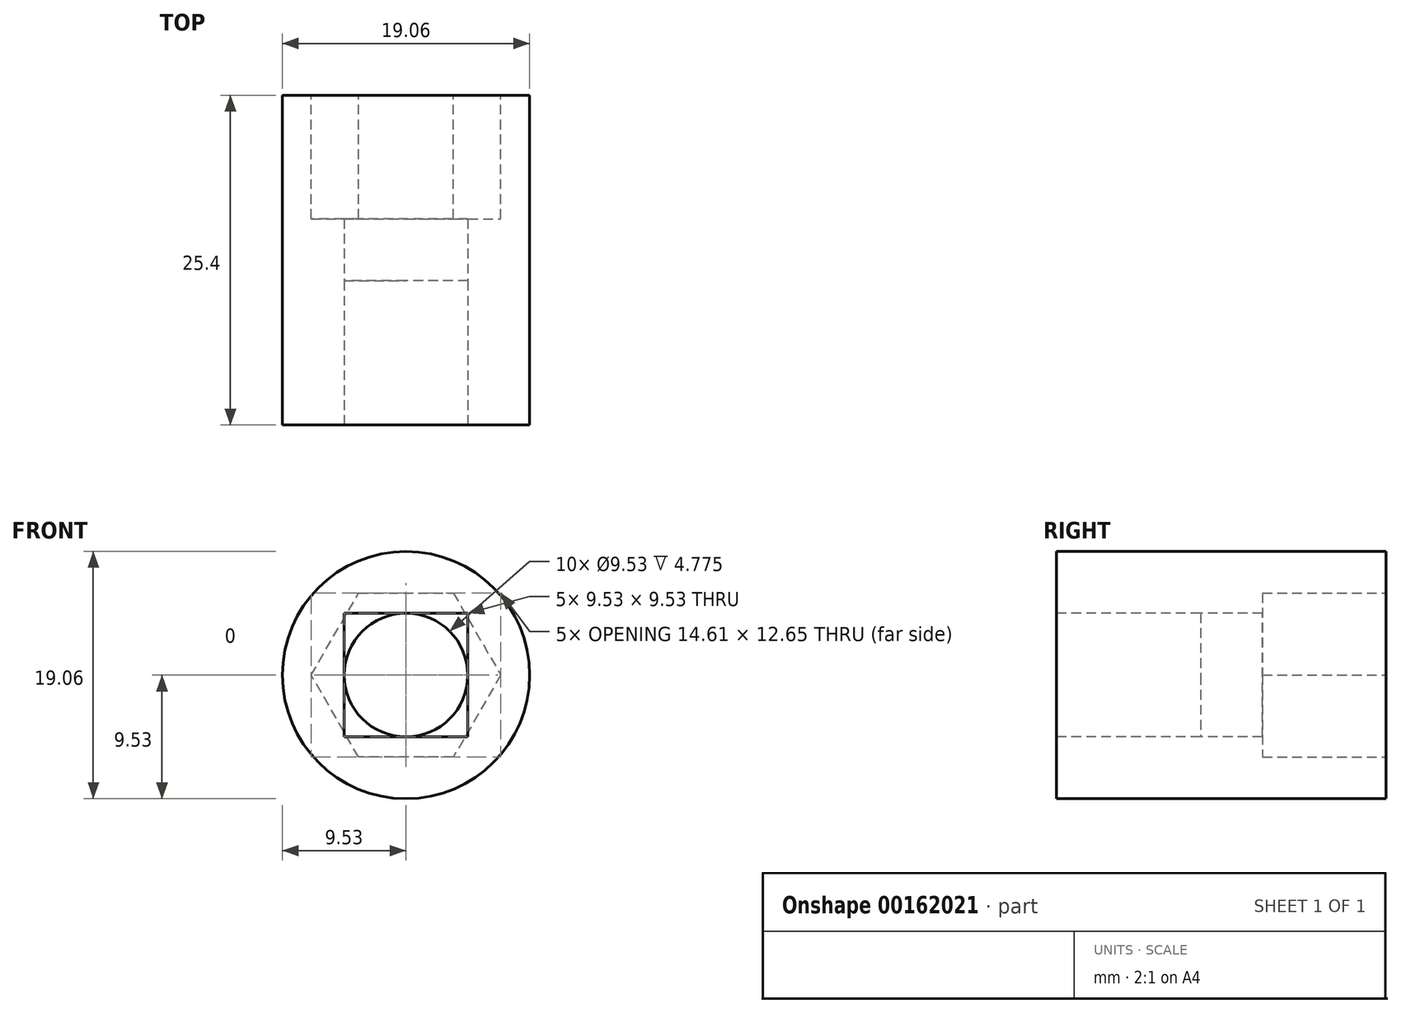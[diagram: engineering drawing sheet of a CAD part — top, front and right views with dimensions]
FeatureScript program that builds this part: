
annotation { "Feature Type Name" : "Feature", "Feature Type Description" : "" }
export const myFeature = defineFeature(function(context is Context, id is Id, definition is map)
    precondition{}
    {
        {
            var Q0;
            Q0=qCreatedBy(makeId("Front.planeOp"),FACE);
            var sketch = newSketch(context, id + "F0", { "sketchPlane" : qUnion([Q0])});
            skCircle(sketch, "E0", {"center": v(0, 0) * mm, "radius": 9.53 * mm});
            skSolve(sketch);
        }
        {
            var Q0;
            Q0 = qSketchRegion(id + "F0", true);
            extrude(context, id + "F1", {"entities" : qUnion([Q0]), "depth" : 25.4 * mm});
        }
        {
            var Q0;
            Q0=makeQuery(id+"F1.opExtrude","CAP_FACE",FACE,{"disambiguationData":[OSD([sQuery(id+"F0.wireOp",EDGE,"E0")])],"isStart":false});
            var sketch = newSketch(context, id + "F2", { "sketchPlane" : qUnion([Q0])});
            skLineSegment(sketch, "E1.bottom", {"start": v(4.76, 4.76) * mm, "end": v(-4.76, 4.76) * mm});
            skLineSegment(sketch, "E1.top", {"start": v(4.76, -4.76) * mm, "end": v(-4.76, -4.76) * mm});
            skLineSegment(sketch, "E1.left", {"start": v(4.76, 4.76) * mm, "end": v(4.76, -4.76) * mm});
            skLineSegment(sketch, "E1.right", {"start": v(-4.76, 4.76) * mm, "end": v(-4.76, -4.76) * mm});
            skPoint(sketch, "E1.middle", {"position": v(0, 0) * mm});
            skCircle(sketch, "E2", {"center": v(0, 0) * mm, "radius": 4.76 * mm});
            skSolve(sketch);
        }
        {
            var Q0;
            {var subQ0=sQuery(id+"F2.wireOp",EDGE,"E2");var subQ1=makeQuery(id+"F2.imprint","INTERSECT",VERTEX,{"derivedFrom":[sQuery(id+"F2.wireOp",EDGE,"E1.bottom"),subQ0]});Q0=makeQuery(id+"F2.imprint","IMPRINT",FACE,{"disambiguationData":[TD([[makeQuery(id+"F2.imprint","IMPRINT",EDGE,{"disambiguationData":[TD([[subQ1,1.0]])],"derivedFrom":subQ0}),1.0]])]});}
            var Q1;
            Q1=sQuery(id+"F2.wireOp",EDGE,"E2");
            extrude(context, id + "F3", {"entities" : qUnion([Q0]), "operationType" : NewBodyOperationType.REMOVE, "surfaceEntities" : qUnion([Q1]), "endBound" : BoundingType.THROUGH_ALL, "oppositeDirection" : true, "depth" : 25.4 * mm});
        }
        {
            var Q0;
            Q0 = qSketchRegion(id + "F2", true);
            extrude(context, id + "F4", {"entities" : qUnion([Q0]), "operationType" : NewBodyOperationType.REMOVE, "oppositeDirection" : true, "depth" : 11.1 * mm});
        }
        {
            var Q0;
            Q0=qCreatedBy(makeId("Front.planeOp"),FACE);
            var sketch = newSketch(context, id + "F5", { "sketchPlane" : qUnion([Q0])});
            skCircle(sketch, "E3.cCircle", {"center": v(0, 0) * mm, "radius": 6.32 * mm, "construction": true});
            skLineSegment(sketch, "E3.0", {"start": v(-3.65, 6.32) * mm, "end": v(3.65, 6.32) * mm});
            skLineSegment(sketch, "E3.1", {"start": v(3.65, 6.32) * mm, "end": v(7.3, 0) * mm});
            skLineSegment(sketch, "E3.2", {"start": v(7.3, 0) * mm, "end": v(3.65, -6.32) * mm});
            skLineSegment(sketch, "E3.3", {"start": v(3.65, -6.32) * mm, "end": v(-3.65, -6.32) * mm});
            skLineSegment(sketch, "E3.4", {"start": v(-3.65, -6.32) * mm, "end": v(-7.3, 0) * mm});
            skLineSegment(sketch, "E3.5", {"start": v(-7.3, 0) * mm, "end": v(-3.65, 6.32) * mm});
            skPoint(sketch, "E3.0.midPoint", {"position": v(0, 6.32) * mm});
            skSolve(sketch);
        }
        {
            var Q0;
            Q0 = qSketchRegion(id + "F5", true);
            extrude(context, id + "F6", {"entities" : qUnion([Q0]), "operationType" : NewBodyOperationType.REMOVE, "depth" : 9.52 * mm});
        }
    });
